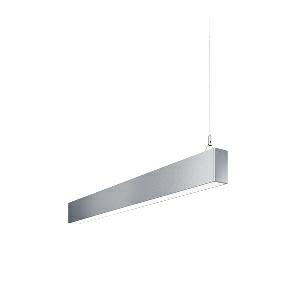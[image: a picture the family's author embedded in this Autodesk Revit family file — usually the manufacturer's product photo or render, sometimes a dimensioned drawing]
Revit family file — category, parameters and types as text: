
# Revit family: idoo_line_-_ilp_2000_vtl_d_end_00806463_e457
name_source: partatom
category: Lighting Fixtures
units: mm (PartAtom-declared; Revit-internal decimal feet)

## family parameters
Cut with Voids When Loaded = No
Host = Face
Light Source = No
Part Type = Normal
Room Calculation Point = No
Round Connector Dimension = Use Diameter
Shared = No

## types (1)
- IDOO.line - ILP 2000/VTL/D END (1 x LED, 2300 lm, 2700-6500K)
    Apparent Load = 23 VA
    Approval mark = CE
    CIE Flux Codes = 66 91 98 40 100
    Color Rendering = 90-100
    Color Temperature = 2700-6500K
    Control Gear = Electronic ballast
    Default Elevation = 1800 mm
    Description = ILP 2000/VTL/D|Suspended luminaire|light source: LED|connected load: 220-240 V, 50/60 Hz|Power consumption: approx. 23 W|standby: approx. 0,25|luminous flux: 2300 lm|luminous efficacy: 100 lm/W|light distribution: Direct/indirect|direct ratio: approx. 40 %|colour temperature: Cold white, ca. 2700-6500 K|color rendering index (CRI): >= 90|chromaticity tolerance:  3 SDCM|System of protection: IP 40|technology: Continuously dimmable|luminaire body|material: Sectional aluminium|colour: Silver|lamp cover: Acrylic (PMMA), Clear|mains lead: 1,0 m With free stranded wires|Fastening: Steel cable 0.3 - 0.7 m|glare control: Prism aperture|luminance(L65): <= 2700 cd/m|unified glare rating(4H 8H): <=  16|special features: Specified values at approx. 4000 K, DALI Load 1x, Through-wired, up to 18 m on one mains connection, External control required for Dali Device type 8, Flicker-free, Constant luminous flux between 2700 and 6500 K, Constant colour temperature over the whole dimming range, Suitable as emergency lighting, Mechanical and electrical connection of the individual modules without tools|
    Frequency = 50 Hz
    Height = 110 mm
    Lamp = 1 x LED
    Lamp Light Flux = 2300 lm
    Lamp count = 1
    Length = 848 mm
    Luminous efficacy = 100 lm/W
    Manufacturer = Waldmann
    ModVariant = No
    Model = 00806463
    Mounting Place = Ceiling
    Mounting Type = Pendant
    Number of Poles = 1
    OnlyDefault = Yes
    Power Factor = 1
    Product Name = IDOO.line - ILP 2000/VTL/D END
    Product group = Suspended luminaire
    ProductGroupID = 9
    Protection Class = Protection class I
    Protection Degree = IP 40
    RLX_Detail_Level = 1
    RLX_Emergency_Light_Flux = 0 lm
    RLX_Emergency_Type = 0
    RLX_Emergency_Type_DB = No
    RlxData = <blob elided: 18925 chars, md5=04b2d552>
    Socket = socket
    Standby Power = 0 W
    System Light Flux = 2300 lm
    System Power = 23 W
    Type Comments = Product without accessories
    Type Image = 113300000-00692564.jpg
    URL = http://relux.com
    VarID = ---
    Voltage = 230 V
    Voltage Range = 220-240 V
    Weight = 0.00 kg
    Width = 60 mm  [stored 0.19685 ft]

note: [stored X ft] marks values corroborated as IEEE doubles in the binary element streams (Revit-internal decimal feet)

## geometry (parser evidence)
native form markers: Blend x4, Sweep x13
no freeform markers — native parametric forms only
